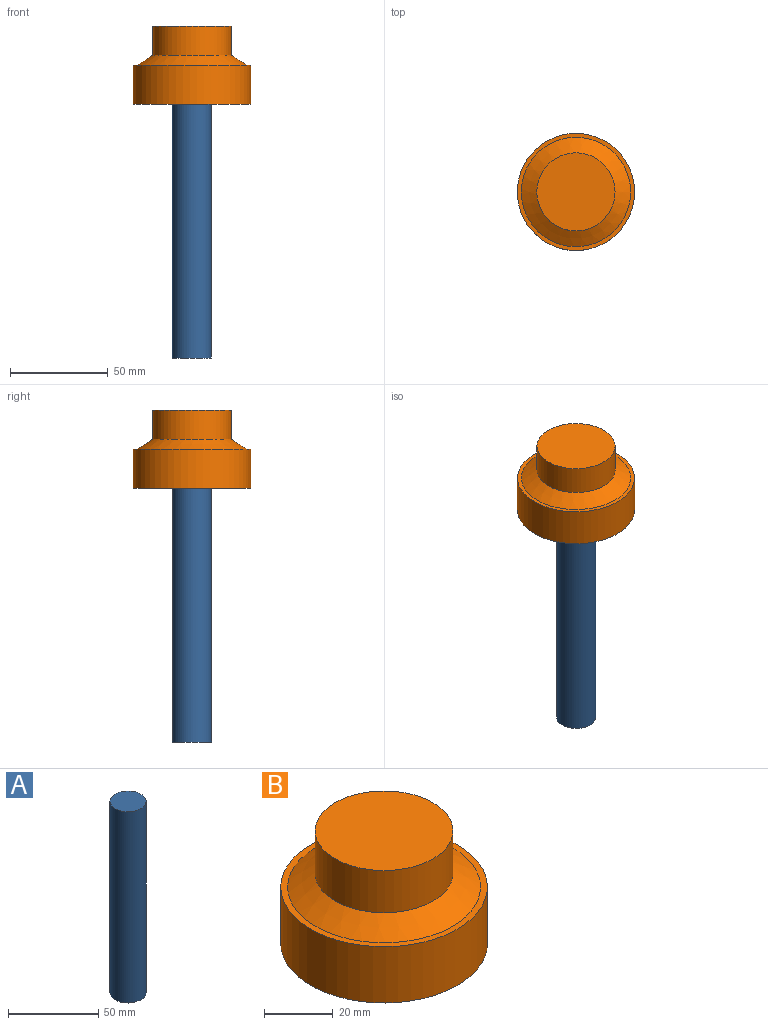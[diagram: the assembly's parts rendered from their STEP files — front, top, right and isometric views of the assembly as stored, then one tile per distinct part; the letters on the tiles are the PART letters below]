
ASSEMBLY  parts=2 mates=1
PART A: 3 faces, bbox 20x20x130 mm
  f0: cylinder r=10mm len=130mm, axis (0,0,-1), area 8168.1mm2, adj f1,f2
  f1: plane 20x20mm, normal (0,0,1), area 314.2mm2, adj f0
  f2: plane 20x20mm, normal (0,0,-1), area 314.2mm2, adj f0
PART B: 6 faces, bbox 60x60x40 mm
  f0: cylinder r=20mm len=40mm, axis (0,0,-1), area 1885mm2, adj f1,f5
  f1: plane 40x40mm, normal (0,0,1), area 1256.6mm2, adj f0
  f2: plane 60x60mm, normal (0,0,1), area 364.4mm2, adj f4,f5
  f3: plane 60x60mm, normal (0,0,-1), area 2827.4mm2, adj f4
  f4: cylinder r=30mm len=60mm, axis (0,0,-1), area 3769.9mm2, adj f2,f3
  f5: cone r=20mm half-angle=58deg, axis (0,0,-1), area 1422.6mm2, adj f0,f2
PLACE A t=(-37.05,4.09,-26.78)mm
PLACE B t=(-12.05,4.09,603.22)mm
MATE parallel B.f4 <-> A.f0  axis (0,0,-1) through (-37.05,4.09,103.22)mm
